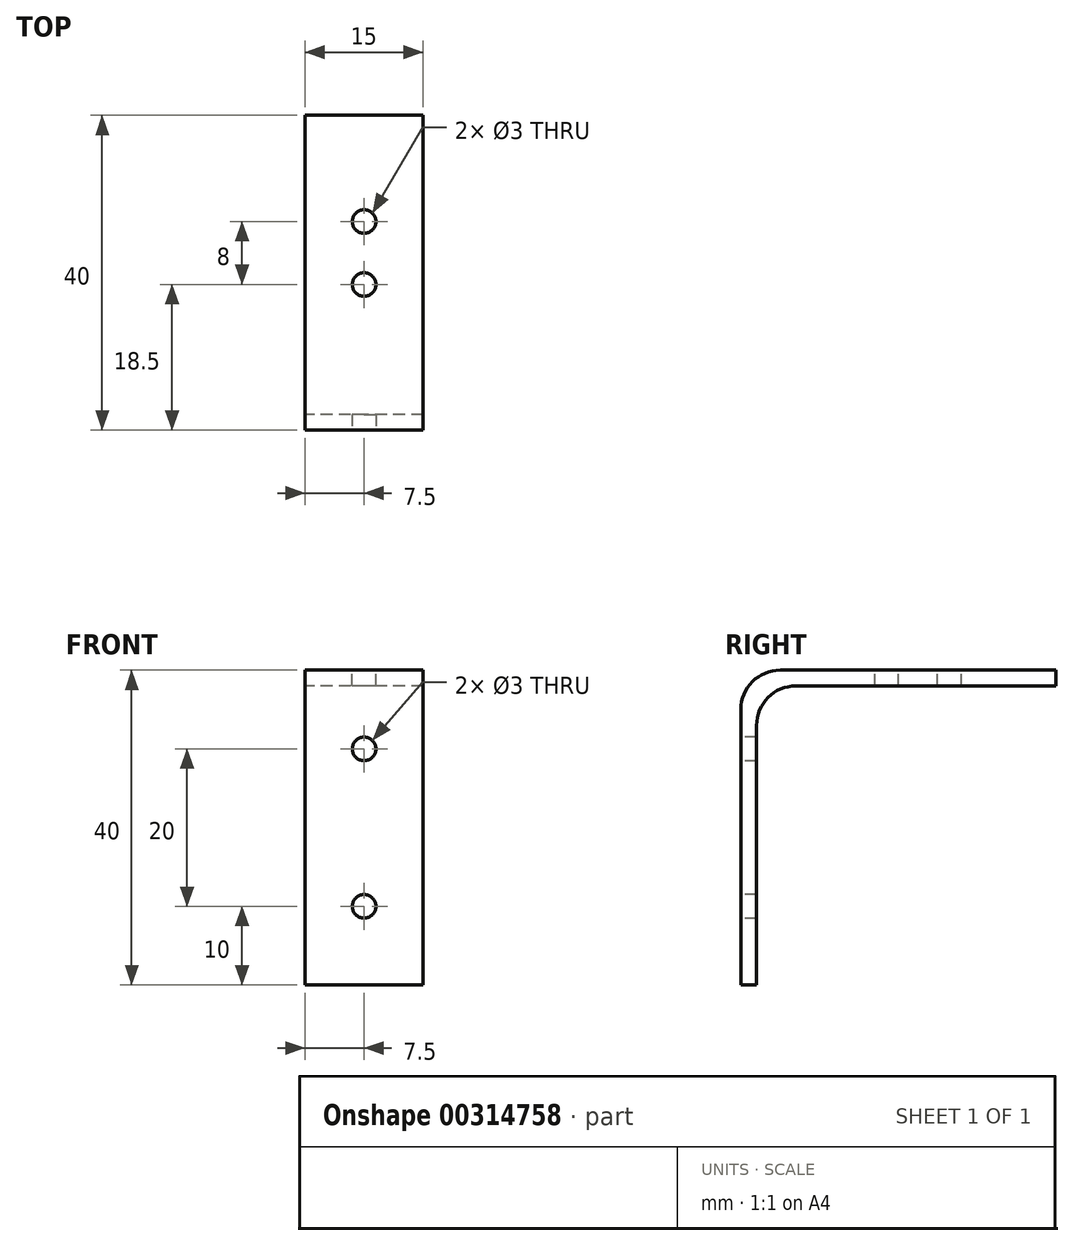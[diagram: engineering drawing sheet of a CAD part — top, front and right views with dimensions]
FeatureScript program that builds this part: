
annotation { "Feature Type Name" : "Feature", "Feature Type Description" : "" }
export const myFeature = defineFeature(function(context is Context, id is Id, definition is map)
    precondition{}
    {
        {
            var Q0;
            Q0=qCreatedBy(makeId("Right.planeOp"),FACE);
            var sketch = newSketch(context, id + "F0", { "sketchPlane" : qUnion([Q0])});
            skLineSegment(sketch, "E0.top", {"start": v(0, -38) * mm, "end": v(-2, -38) * mm});
            skLineSegment(sketch, "E0.left", {"start": v(0, 0) * mm, "end": v(0, -38) * mm});
            skLineSegment(sketch, "E0.right", {"start": v(-2.4, 0) * mm, "end": v(-2.4, 0) * mm});
            skLineSegment(sketch, "E1.bottom", {"start": v(0, 0) * mm, "end": v(38, 0) * mm});
            skLineSegment(sketch, "E1.top", {"start": v(-2, 2) * mm, "end": v(38, 2) * mm});
            skLineSegment(sketch, "E1.right", {"start": v(38, 0) * mm, "end": v(38, 2) * mm});
            skLineSegment(sketch, "E2", {"start": v(-2, 2) * mm, "end": v(-2, -38) * mm});
            skSolve(sketch);
        }
        {
            var Q0;
            Q0=makeQuery(id+"F0.imprint","IMPRINT",FACE,{"disambiguationData":[TD([[makeQuery(id+"F0.imprint","IMPRINT",EDGE,{"derivedFrom":sQuery(id+"F0.wireOp",EDGE,"E0.top")}),-1.0]])]});
            extrude(context, id + "F1", {"entities" : qUnion([Q0]), "depth" : 15 * mm, "offsetDistance" : 25 * mm});
        }
        {
            var Q0;
            Q0=makeQuery(id+"F1.opExtrude","SWEPT_EDGE",EDGE,{"disambiguationData":[OSD([sQuery(id+"F0.wireOp",EDGE,"E1.top"),sQuery(id+"F0.wireOp",EDGE,"E2")])]});
            fillet(context, id + "F2", {"entities" : qUnion([Q0]), "radius" : 5 * mm, "tangentPropagation" : true, "allowEdgeOverflow" : false});
        }
        {
            var Q0;
            Q0=makeQuery(id+"F1.opExtrude","SWEPT_EDGE",EDGE,{"disambiguationData":[OSD([sQuery(id+"F0.wireOp",EDGE,"E0.left"),sQuery(id+"F0.wireOp",EDGE,"E1.bottom")])]});
            fillet(context, id + "F3", {"entities" : qUnion([Q0]), "radius" : 5 * mm, "tangentPropagation" : true, "allowEdgeOverflow" : false});
        }
        {
            var Q0;
            Q0=makeQuery(id+"F1.opExtrude","SWEPT_FACE",FACE,{"disambiguationData":[OSD([sQuery(id+"F0.wireOp",EDGE,"E1.top")])]});
            var sketch = newSketch(context, id + "F4", { "sketchPlane" : qUnion([Q0])});
            skPoint(sketch, "E3.centerSnap0", {"position": v(15, 20.5) * mm});
            skPoint(sketch, "E3.centerSnap1", {"position": v(7.5, 38) * mm});
            skCircle(sketch, "E4", {"center": v(7.5, 24.5) * mm, "radius": 1.5 * mm});
            skCircle(sketch, "E5", {"center": v(7.5, 16.5) * mm, "radius": 1.5 * mm});
            skPoint(sketch, "E3.center.orphan", {"position": v(7.5, 20.5) * mm});
            skLineSegment(sketch, "E6", {"start": v(7.5, 38) * mm, "end": v(7.5, 24.5) * mm});
            skLineSegment(sketch, "E7", {"start": v(7.5, 24.5) * mm, "end": v(7.5, 16.5) * mm});
            skSolve(sketch);
        }
        {
            var Q0;
            Q0=sQuery(id+"F4.wireOp",VERTEX,"E4.center");
            var Q1;
            Q1=sQuery(id+"F4.wireOp",VERTEX,"E5.center");
            var Q2;
            Q2=makeQuery(id+"F1.opExtrude","SWEPT_BODY",BODY,{"disambiguationData":[OSD([sQuery(id+"F0.wireOp",EDGE,"E0.top"),sQuery(id+"F0.wireOp",EDGE,"E0.left"),sQuery(id+"F0.wireOp",EDGE,"E1.bottom"),sQuery(id+"F0.wireOp",EDGE,"E1.top"),sQuery(id+"F0.wireOp",EDGE,"E1.right"),sQuery(id+"F0.wireOp",EDGE,"E2")])]});
            hole(context, id + "F5", {"style" : HoleStyle.SIMPLE, "endStyle" : HoleEndStyle.THROUGH, "holeDiameter" : 3 * mm, "isTappedThrough" : true, "tappedDepth" : 12 * mm, "tapClearance" : 3, "locations" : qUnion([Q0, Q1]), "scope" : qUnion([Q2]), "majorDiameter" : 5 * mm});
        }
        {
            var Q0;
            Q0=makeQuery(id+"F1.opExtrude","SWEPT_FACE",FACE,{"disambiguationData":[OSD([sQuery(id+"F0.wireOp",EDGE,"E2")])]});
            var sketch = newSketch(context, id + "F6", { "sketchPlane" : qUnion([Q0])});
            skCircle(sketch, "E8", {"center": v(7.5, -28) * mm, "radius": 1.5 * mm});
            skCircle(sketch, "E9", {"center": v(7.5, -8) * mm, "radius": 1.5 * mm});
            skPoint(sketch, "E10.orphan", {"position": v(7.5, -3) * mm});
            skPoint(sketch, "E11.orphan", {"position": v(7.5, -38) * mm});
            skLineSegment(sketch, "E12", {"start": v(7.5, -8) * mm, "end": v(15, -8) * mm});
            skLineSegment(sketch, "E13", {"start": v(7.5, -8) * mm, "end": v(0, -8) * mm});
            skLineSegment(sketch, "E14", {"start": v(7.5, -28) * mm, "end": v(0, -28) * mm});
            skLineSegment(sketch, "E15", {"start": v(7.5, -28) * mm, "end": v(7.5, -38) * mm});
            skLineSegment(sketch, "E16", {"start": v(7.5, -8) * mm, "end": v(7.5, -28) * mm});
            skSolve(sketch);
        }
        {
            var Q0;
            Q0=sQuery(id+"F6.wireOp",VERTEX,"E9.center");
            var Q1;
            Q1=sQuery(id+"F6.wireOp",VERTEX,"E8.center");
            var Q2;
            Q2=makeQuery(id+"F1.opExtrude","SWEPT_BODY",BODY,{"disambiguationData":[OSD([sQuery(id+"F0.wireOp",EDGE,"E0.top"),sQuery(id+"F0.wireOp",EDGE,"E0.left"),sQuery(id+"F0.wireOp",EDGE,"E1.bottom"),sQuery(id+"F0.wireOp",EDGE,"E1.top"),sQuery(id+"F0.wireOp",EDGE,"E1.right"),sQuery(id+"F0.wireOp",EDGE,"E2")])]});
            hole(context, id + "F7", {"style" : HoleStyle.SIMPLE, "endStyle" : HoleEndStyle.THROUGH, "holeDiameter" : 3 * mm, "isTappedThrough" : true, "tappedDepth" : 12 * mm, "tapClearance" : 3, "locations" : qUnion([Q0, Q1]), "scope" : qUnion([Q2]), "majorDiameter" : 5 * mm});
        }
    });
